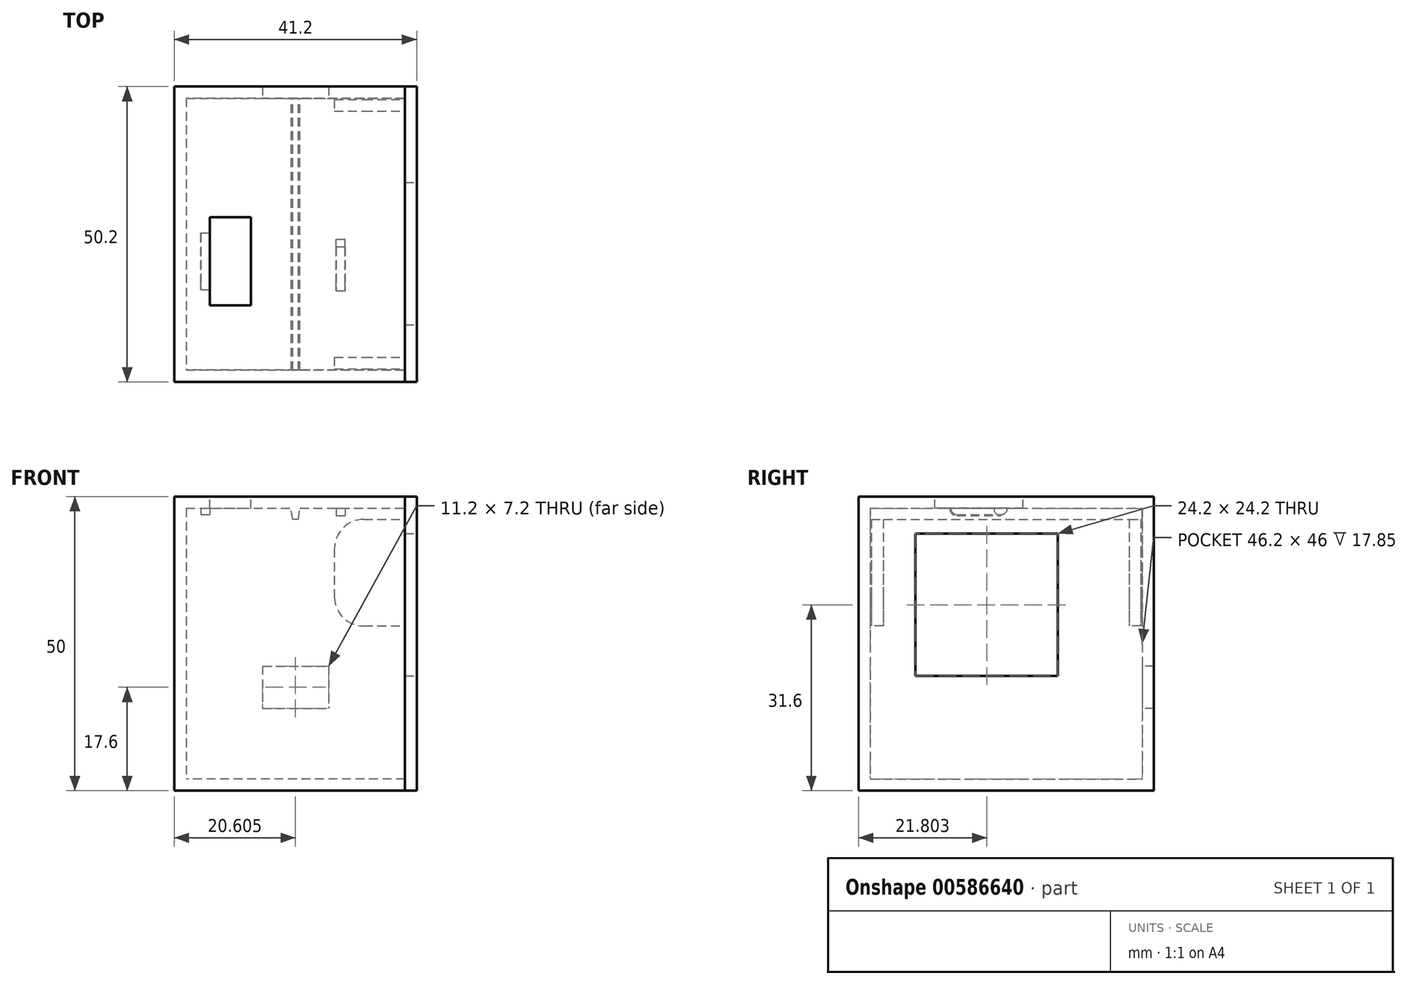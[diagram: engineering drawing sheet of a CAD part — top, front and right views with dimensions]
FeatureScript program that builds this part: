
annotation { "Feature Type Name" : "Feature", "Feature Type Description" : "" }
export const myFeature = defineFeature(function(context is Context, id is Id, definition is map)
    precondition{}
    {
        {
            var Q0;
            Q0=qCreatedBy(makeId("Top.planeOp"),FACE);
            var sketch = newSketch(context, id + "F0", { "sketchPlane" : qUnion([Q0])});
            skLineSegment(sketch, "E0.bottom", {"start": v(-20.75, 21) * mm, "end": v(14.45, 21) * mm});
            skLineSegment(sketch, "E0.top", {"start": v(-20.75, -25.2) * mm, "end": v(14.45, -25.2) * mm});
            skLineSegment(sketch, "E0.left", {"start": v(-20.75, 21) * mm, "end": v(-20.75, -25.2) * mm});
            skLineSegment(sketch, "E0.right", {"start": v(14.45, 21) * mm, "end": v(14.45, -25.2) * mm});
            skLineSegment(sketch, "E1.0", {"start": v(-22.75, -27.2) * mm, "end": v(16.45, -27.2) * mm});
            skLineSegment(sketch, "E1.1", {"start": v(-22.75, 23) * mm, "end": v(-22.75, -27.2) * mm});
            skLineSegment(sketch, "E1.2", {"start": v(-22.75, 23) * mm, "end": v(16.45, 23) * mm});
            skLineSegment(sketch, "E1.3", {"start": v(16.45, 23) * mm, "end": v(16.45, -27.2) * mm});
            skSolve(sketch);
        }
        {
            var Q0;
            Q0=makeQuery(id+"F0.imprint","IMPRINT",FACE,{"disambiguationData":[TD([[makeQuery(id+"F0.imprint","IMPRINT",EDGE,{"derivedFrom":sQuery(id+"F0.wireOp",EDGE,"E0.bottom")}),-1.0]])]});
            var Q1;
            Q1=makeQuery(id+"F0.imprint","IMPRINT",FACE,{"disambiguationData":[TD([[makeQuery(id+"F0.imprint","IMPRINT",EDGE,{"derivedFrom":sQuery(id+"F0.wireOp",EDGE,"E0.bottom")}),1.0]])]});
            extrude(context, id + "F1", {"entities" : qUnion([Q0, Q1]), "depth" : 2 * mm, "offsetDistance" : 25 * mm});
        }
        {
            var Q0;
            Q0=makeQuery(id+"F0.imprint","IMPRINT",FACE,{"disambiguationData":[TD([[makeQuery(id+"F0.imprint","IMPRINT",EDGE,{"derivedFrom":sQuery(id+"F0.wireOp",EDGE,"E0.bottom")}),1.0]])]});
            extrude(context, id + "F2", {"entities" : qUnion([Q0]), "operationType" : NewBodyOperationType.ADD, "depth" : (2 + 46 + 2) * mm, "offsetDistance" : 25 * mm});
        }
        {
            var Q0;
            {var subQ0=sQuery(id+"F0.wireOp",EDGE,"E1.3");Q0=makeQuery(id+"F2.boolean.opBoolean","MERGE",FACE,{"derivedFrom":[makeQuery(id+"F1.opExtrude","SWEPT_FACE",FACE,{"disambiguationData":[OSD([subQ0])]}),makeQuery(id+"F2.opExtrude","SWEPT_FACE",FACE,{"disambiguationData":[OSD([subQ0])]})]});}
            var sketch = newSketch(context, id + "F3", { "sketchPlane" : qUnion([Q0])});
            skLineSegment(sketch, "E2.0", {"start": v(23, 50) * mm, "end": v(-27.2, 50) * mm});
            skLineSegment(sketch, "E2.1", {"start": v(-27.2, 50) * mm, "end": v(-27.2, 0) * mm});
            skLineSegment(sketch, "E2.2", {"start": v(23, 0) * mm, "end": v(-27.2, 0) * mm});
            skLineSegment(sketch, "E2.3", {"start": v(23, 50) * mm, "end": v(23, 0) * mm});
            skLineSegment(sketch, "E3.0", {"start": v(-25.2, 48) * mm, "end": v(-25.2, 2) * mm});
            skLineSegment(sketch, "E3.1", {"start": v(21, 48) * mm, "end": v(-25.2, 48) * mm});
            skLineSegment(sketch, "E3.2", {"start": v(21, 48) * mm, "end": v(21, 2) * mm});
            skLineSegment(sketch, "E3.3", {"start": v(21, 2) * mm, "end": v(-25.2, 2) * mm});
            skLineSegment(sketch, "E4.0", {"start": v(21, 44) * mm, "end": v(-25.2, 44) * mm});
            skSolve(sketch);
        }
        {
            var Q0;
            {var subQ8=sQuery(id+"F3.wireOp",EDGE,"E4.0");Q0=makeQuery(id+"F3.imprint","IMPRINT",FACE,{"disambiguationData":[TD([[makeQuery(id+"F3.imprint","IMPRINT",EDGE,{"derivedFrom":subQ8}),-1.0]])]});}
            var Q1;
            {var subQ0=sQuery(id+"F3.wireOp",EDGE,"E3.3");Q1=makeQuery(id+"F3.imprint","IMPRINT",FACE,{"disambiguationData":[TD([[makeQuery(id+"F3.imprint","IMPRINT",EDGE,{"derivedFrom":subQ0}),-1.0]])]});}
            extrude(context, id + "F4", {"entities" : qUnion([Q0, Q1]), "operationType" : NewBodyOperationType.REMOVE, "oppositeDirection" : true, "depth" : 25 * mm, "offsetDistance" : 25 * mm});
        }
        {
            var Q0;
            Q0=makeQuery(id+"F2.opExtrude","CAP_FACE",FACE,{"disambiguationData":[OSD([sQuery(id+"F0.wireOp",EDGE,"E0.bottom"),sQuery(id+"F0.wireOp",EDGE,"E0.top"),sQuery(id+"F0.wireOp",EDGE,"E0.left"),sQuery(id+"F0.wireOp",EDGE,"E0.right"),sQuery(id+"F0.wireOp",EDGE,"E1.0"),sQuery(id+"F0.wireOp",EDGE,"E1.1"),sQuery(id+"F0.wireOp",EDGE,"E1.2"),sQuery(id+"F0.wireOp",EDGE,"E1.3")])],"isStart":false});
            var sketch = newSketch(context, id + "F5", { "sketchPlane" : qUnion([Q0])});
            skLineSegment(sketch, "E5.0", {"start": v(-20.75, 21) * mm, "end": v(-20.75, -25.2) * mm});
            skLineSegment(sketch, "E5.1", {"start": v(-20.75, -25.2) * mm, "end": v(14.45, -25.2) * mm});
            skLineSegment(sketch, "E5.2", {"start": v(14.45, 21) * mm, "end": v(14.45, -25.2) * mm});
            skLineSegment(sketch, "E5.3", {"start": v(-20.75, 21) * mm, "end": v(14.45, 21) * mm});
            skLineSegment(sketch, "E6.bottom", {"start": v(-16.75, 0.8) * mm, "end": v(-9.75, 0.8) * mm});
            skLineSegment(sketch, "E6.top", {"start": v(-16.75, -14.2) * mm, "end": v(-9.75, -14.2) * mm});
            skLineSegment(sketch, "E6.left", {"start": v(-16.75, 0.8) * mm, "end": v(-16.75, -14.2) * mm});
            skLineSegment(sketch, "E6.right", {"start": v(-9.75, 0.8) * mm, "end": v(-9.75, -14.2) * mm});
            skSolve(sketch);
        }
        {
            var Q0;
            Q0=makeQuery(id+"F5.imprint","IMPRINT",FACE,{"disambiguationData":[TD([[makeQuery(id+"F5.imprint","IMPRINT",EDGE,{"derivedFrom":sQuery(id+"F5.wireOp",EDGE,"E5.0")}),1.0]])]});
            extrude(context, id + "F6", {"entities" : qUnion([Q0]), "operationType" : NewBodyOperationType.ADD, "oppositeDirection" : true, "depth" : 2 * mm, "offsetDistance" : 25 * mm});
        }
        {
            var Q0;
            Q0=makeQuery(id+"F6.opExtrude","SWEPT_FACE",FACE,{"disambiguationData":[OSD([sQuery(id+"F5.wireOp",EDGE,"E6.left")])]});
            var sketch = newSketch(context, id + "F7", { "sketchPlane" : qUnion([Q0])});
            skLineSegment(sketch, "E7.0", {"start": v(0.8, 48) * mm, "end": v(-6.7, 48) * mm});
            skPoint(sketch, "E8", {"position": v(-6.7, 48) * mm});
            skLineSegment(sketch, "E9", {"start": v(-6.7, 48) * mm, "end": v(-14.2, 48) * mm});
            skPoint(sketch, "E10", {"position": v(-10.45, 48) * mm});
            skPoint(sketch, "E11", {"position": v(-2.95, 48) * mm});
            skCircle(sketch, "E12", {"center": v(-10.45, 48) * mm, "radius": 1.05 * mm});
            skLineSegment(sketch, "E13", {"start": v(-6.7, 45.3) * mm, "end": v(-6.7, 50) * mm, "construction": true});
            skCircle(sketch, "E14.MirrorC", {"center": v(-2.95, 48) * mm, "radius": 1.05 * mm});
            skLineSegment(sketch, "E15", {"start": v(-10.45, 48) * mm, "end": v(-10.45, 46.06) * mm, "construction": true});
            skLineSegment(sketch, "E16.MirrorCS", {"start": v(-2.95, 48) * mm, "end": v(-2.95, 46.06) * mm, "construction": true});
            skLineSegment(sketch, "E17", {"start": v(-10.45, 46.95) * mm, "end": v(-2.95, 46.95) * mm});
            skPoint(sketch, "E17.startSnap0", {"position": v(-10.45, 47.03) * mm});
            skSolve(sketch);
        }
        {
            var Q0;
            {var subQ0=sQuery(id+"F7.wireOp",EDGE,"E17");Q0=makeQuery(id+"F7.imprint","IMPRINT",FACE,{"disambiguationData":[TD([[makeQuery(id+"F7.imprint","IMPRINT",EDGE,{"derivedFrom":subQ0}),1.0]])]});}
            var Q1;
            {var subQ0=sQuery(id+"F7.wireOp",EDGE,"E14.MirrorC");var subQ1=sQuery(id+"F7.wireOp",EDGE,"E7.0");var subQ2=makeQuery(id+"F7.imprint","INTERSECT",VERTEX,{"disambiguationData":[OD(0.0)],"derivedFrom":[subQ1,subQ0]});Q1=makeQuery(id+"F7.imprint","IMPRINT",FACE,{"disambiguationData":[TD([[makeQuery(id+"F7.imprint","IMPRINT",EDGE,{"disambiguationData":[TD([[subQ2,-1.0]])],"derivedFrom":subQ1}),1.0]])]});}
            var Q2;
            {var subQ0=sQuery(id+"F7.wireOp",EDGE,"E12");var subQ1=sQuery(id+"F7.wireOp",EDGE,"E9");var subQ2=makeQuery(id+"F7.imprint","INTERSECT",VERTEX,{"disambiguationData":[OD(0.0)],"derivedFrom":[subQ1,subQ0]});Q2=makeQuery(id+"F7.imprint","IMPRINT",FACE,{"disambiguationData":[TD([[makeQuery(id+"F7.imprint","IMPRINT",EDGE,{"disambiguationData":[TD([[subQ2,1.0]])],"derivedFrom":subQ1}),1.0]])]});}
            extrude(context, id + "F8", {"entities" : qUnion([Q0, Q1, Q2]), "operationType" : NewBodyOperationType.ADD, "oppositeDirection" : true, "depth" : 1.5 * mm, "offsetDistance" : 25 * mm});
        }
        {
            var Q0;
            Q0=makeQuery(id+"F4.boolean.opBoolean","MERGE",FACE,{"derivedFrom":[makeQuery(id+"F2.opExtrude","SWEPT_FACE",FACE,{"disambiguationData":[OSD([sQuery(id+"F0.wireOp",EDGE,"E0.bottom")])]}),makeQuery(id+"F4.opExtrude","SWEPT_FACE",FACE,{"disambiguationData":[OSD([sQuery(id+"F3.wireOp",EDGE,"E3.2")])]})]});
            var sketch = newSketch(context, id + "F9", { "sketchPlane" : qUnion([Q0])});
            skPoint(sketch, "E18", {"position": v(-2.15, 48) * mm});
            skLineSegment(sketch, "E19", {"start": v(-2.15, 40.55) * mm, "end": v(-2.15, 51.7) * mm, "construction": true});
            skPoint(sketch, "E20.endSnap0", {"position": v(-2.15, 46.13) * mm});
            skLineSegment(sketch, "E21", {"start": v(-2.15, 46.13) * mm, "end": v(-2.65, 46.13) * mm});
            skLineSegment(sketch, "E22", {"start": v(-2.65, 46.13) * mm, "end": v(-2.9, 48) * mm});
            skLineSegment(sketch, "E23", {"start": v(-2.9, 48) * mm, "end": v(-2.15, 48) * mm});
            skLineSegment(sketch, "E24.MirrorCS", {"start": v(-2.15, 46.13) * mm, "end": v(-1.65, 46.13) * mm});
            skLineSegment(sketch, "E25.MirrorCS", {"start": v(-1.4, 48) * mm, "end": v(-2.15, 48) * mm});
            skLineSegment(sketch, "E26.MirrorCS", {"start": v(-1.65, 46.13) * mm, "end": v(-1.4, 48) * mm});
            skSolve(sketch);
        }
        {
            var Q0;
            Q0=makeQuery(id+"F9.imprint","IMPRINT",FACE,{"disambiguationData":[TD([[makeQuery(id+"F9.imprint","IMPRINT",EDGE,{"derivedFrom":sQuery(id+"F9.wireOp",EDGE,"E21")}),-1.0]])]});
            extrude(context, id + "F10", {"entities" : qUnion([Q0]), "operationType" : NewBodyOperationType.ADD, "endBound" : BoundingType.UP_TO_NEXT, "depth" : 25 * mm, "offsetDistance" : 25 * mm});
        }
        {
            var Q0;
            {var subQ0=sQuery(id+"F0.wireOp",EDGE,"E1.3");Q0=makeQuery(id+"F2.boolean.opBoolean","MERGE",FACE,{"derivedFrom":[makeQuery(id+"F1.opExtrude","SWEPT_FACE",FACE,{"disambiguationData":[OSD([subQ0])]}),makeQuery(id+"F2.opExtrude","SWEPT_FACE",FACE,{"disambiguationData":[OSD([subQ0])]})]});}
            var sketch = newSketch(context, id + "F11", { "sketchPlane" : qUnion([Q0])});
            skLineSegment(sketch, "E27.0", {"start": v(-27.2, 50) * mm, "end": v(-27.2, 0) * mm});
            skLineSegment(sketch, "E27.1", {"start": v(23, 50) * mm, "end": v(-27.2, 50) * mm});
            skLineSegment(sketch, "E27.2", {"start": v(23, 50) * mm, "end": v(23, 0) * mm});
            skLineSegment(sketch, "E27.3", {"start": v(23, 0) * mm, "end": v(-27.2, 0) * mm});
            skLineSegment(sketch, "E27.4", {"start": v(21, 48) * mm, "end": v(21, 2) * mm});
            skLineSegment(sketch, "E27.5", {"start": v(21, 48) * mm, "end": v(-25.2, 48) * mm});
            skLineSegment(sketch, "E27.6", {"start": v(-25.2, 48) * mm, "end": v(-25.2, 2) * mm});
            skLineSegment(sketch, "E27.7", {"start": v(-25.2, 2) * mm, "end": v(21, 2) * mm});
            skLineSegment(sketch, "E28", {"start": v(21, 28) * mm, "end": v(-25.2, 28) * mm});
            skLineSegment(sketch, "E29", {"start": v(-25, 48) * mm, "end": v(-25, 28) * mm});
            skLineSegment(sketch, "E30", {"start": v(-2.1, 18.33) * mm, "end": v(-2.1, 38.94) * mm, "construction": true});
            skPoint(sketch, "E30.startSnap0", {"position": v(-2.1, 28) * mm});
            skLineSegment(sketch, "E31.MirrorCS", {"start": v(20.8, 48) * mm, "end": v(20.8, 28) * mm});
            skLineSegment(sketch, "E32", {"start": v(-23, 48) * mm, "end": v(-23, 28) * mm});
            skLineSegment(sketch, "E33.MirrorCS", {"start": v(18.8, 48) * mm, "end": v(18.8, 28) * mm});
            skLineSegment(sketch, "E34.0", {"start": v(-25.2, 46.13) * mm, "end": v(21, 46.13) * mm});
            skSolve(sketch);
        }
        {
            var Q0;
            {var subQ1=sQuery(id+"F11.wireOp",EDGE,"E32");var subQ5=sQuery(id+"F11.wireOp",EDGE,"E28");var subQ6=makeQuery(id+"F11.imprint","INTERSECT",VERTEX,{"derivedFrom":[subQ5,subQ1]});Q0=makeQuery(id+"F11.imprint","IMPRINT",FACE,{"disambiguationData":[TD([[makeQuery(id+"F11.imprint","IMPRINT",EDGE,{"disambiguationData":[TD([[subQ6,1.0]])],"derivedFrom":subQ5}),-1.0]])]});}
            var Q1;
            {var subQ0=sQuery(id+"F11.wireOp",EDGE,"E27.5");var subQ1=makeQuery(id+"F4.boolean.opBoolean","COPY",EDGE,{"derivedFrom":makeQuery(id+"F4.opExtrude","CAP_EDGE",EDGE,{"disambiguationData":[OSD([sQuery(id+"F3.wireOp",EDGE,"MNPgkXDO-O9Mw-NbgN-yxrE-MuUepim71a7d")])],"isStart":true})});var subQ2=makeQuery(id+"F11.imprint","INTERSECT",VERTEX,{"disambiguationData":[OD(1.0)],"derivedFrom":[subQ1,subQ0]});Q1=makeQuery(id+"F11.imprint","IMPRINT",FACE,{"disambiguationData":[TD([[makeQuery(id+"F11.imprint","IMPRINT",EDGE,{"disambiguationData":[TD([[subQ2,-1.0]])],"derivedFrom":subQ0}),1.0]])]});}
            var Q2;
            {var subQ0=sQuery(id+"F11.wireOp",EDGE,"E27.5");var subQ1=makeQuery(id+"F4.boolean.opBoolean","COPY",EDGE,{"derivedFrom":makeQuery(id+"F4.opExtrude","CAP_EDGE",EDGE,{"disambiguationData":[OSD([sQuery(id+"F3.wireOp",EDGE,"MNPgkXDO-O9Mw-NbgN-yxrE-MuUepim71a7d")])],"isStart":true})});var subQ2=makeQuery(id+"F11.imprint","INTERSECT",VERTEX,{"disambiguationData":[OD(0.0)],"derivedFrom":[subQ1,subQ0]});Q2=makeQuery(id+"F11.imprint","IMPRINT",FACE,{"disambiguationData":[TD([[makeQuery(id+"F11.imprint","IMPRINT",EDGE,{"disambiguationData":[TD([[subQ2,1.0]])],"derivedFrom":subQ0}),1.0]])]});}
            var Q3;
            {var subQ0=sQuery(id+"F11.wireOp",EDGE,"E34.0");var subQ1=makeQuery(id+"F4.boolean.opBoolean","COPY",EDGE,{"derivedFrom":makeQuery(id+"F4.opExtrude","CAP_EDGE",EDGE,{"disambiguationData":[OSD([sQuery(id+"F3.wireOp",EDGE,"MNPgkXDO-O9Mw-NbgN-yxrE-MuUepim71a7d")])],"isStart":true})});var subQ2=makeQuery(id+"F11.imprint","INTERSECT",VERTEX,{"disambiguationData":[OD(0.0)],"derivedFrom":[subQ1,subQ0]});Q3=makeQuery(id+"F11.imprint","IMPRINT",FACE,{"disambiguationData":[TD([[makeQuery(id+"F11.imprint","IMPRINT",EDGE,{"disambiguationData":[TD([[subQ2,-1.0]])],"derivedFrom":subQ0}),-1.0]])]});}
            var Q4;
            Q4=makeQuery(id+"F11.imprint","IMPRINT",FACE,{"disambiguationData":[TD([[makeQuery(id+"F11.imprint","IMPRINT",EDGE,{"derivedFrom":sQuery(id+"F11.wireOp",EDGE,"E27.0")}),1.0]])]});
            var Q5;
            {var subQ4=sQuery(id+"F11.wireOp",EDGE,"E27.7");Q5=makeQuery(id+"F11.imprint","IMPRINT",FACE,{"disambiguationData":[TD([[makeQuery(id+"F11.imprint","IMPRINT",EDGE,{"derivedFrom":subQ4}),-1.0]])]});}
            var Q6;
            {var subQ0=sQuery(id+"F11.wireOp",EDGE,"E28");var subQ1=sQuery(id+"F11.wireOp",EDGE,"E27.4");var subQ2=makeQuery(id+"F11.imprint","INTERSECT",VERTEX,{"derivedFrom":[subQ1,subQ0]});Q6=makeQuery(id+"F11.imprint","IMPRINT",FACE,{"disambiguationData":[TD([[makeQuery(id+"F11.imprint","IMPRINT",EDGE,{"disambiguationData":[TD([[subQ2,1.0]])],"derivedFrom":subQ1}),-1.0]])]});}
            var Q7;
            {var subQ0=sQuery(id+"F11.wireOp",EDGE,"E27.5");var subQ1=makeQuery(id+"F4.boolean.opBoolean","COPY",EDGE,{"derivedFrom":makeQuery(id+"F4.opExtrude","CAP_EDGE",EDGE,{"disambiguationData":[OSD([sQuery(id+"F3.wireOp",EDGE,"MNPgkXDO-O9Mw-NbgN-yxrE-MuUepim71a7d")])],"isStart":true})});var subQ2=makeQuery(id+"F11.imprint","INTERSECT",VERTEX,{"disambiguationData":[OD(0.0)],"derivedFrom":[subQ1,subQ0]});Q7=makeQuery(id+"F11.imprint","IMPRINT",FACE,{"disambiguationData":[TD([[makeQuery(id+"F11.imprint","IMPRINT",EDGE,{"disambiguationData":[TD([[subQ2,-1.0]])],"derivedFrom":subQ0}),1.0]])]});}
            var Q8;
            {var subQ0=sQuery(id+"F11.wireOp",EDGE,"E29");var subQ1=sQuery(id+"F11.wireOp",EDGE,"E28");var subQ2=makeQuery(id+"F11.imprint","INTERSECT",VERTEX,{"derivedFrom":[subQ1,subQ0]});Q8=makeQuery(id+"F11.imprint","IMPRINT",FACE,{"disambiguationData":[TD([[makeQuery(id+"F11.imprint","IMPRINT",EDGE,{"disambiguationData":[TD([[subQ2,1.0]])],"derivedFrom":subQ1}),-1.0]])]});}
            var Q9;
            {var subQ0=sQuery(id+"F11.wireOp",EDGE,"E31.MirrorCS");var subQ1=sQuery(id+"F11.wireOp",EDGE,"E28");var subQ2=makeQuery(id+"F11.imprint","INTERSECT",VERTEX,{"derivedFrom":[subQ1,subQ0]});Q9=makeQuery(id+"F11.imprint","IMPRINT",FACE,{"disambiguationData":[TD([[makeQuery(id+"F11.imprint","IMPRINT",EDGE,{"disambiguationData":[TD([[subQ2,-1.0]])],"derivedFrom":subQ1}),-1.0]])]});}
            var Q10;
            {var subQ0=sQuery(id+"F11.wireOp",EDGE,"E28");var subQ1=sQuery(id+"F11.wireOp",EDGE,"E27.6");var subQ2=makeQuery(id+"F11.imprint","INTERSECT",VERTEX,{"derivedFrom":[subQ1,subQ0]});Q10=makeQuery(id+"F11.imprint","IMPRINT",FACE,{"disambiguationData":[TD([[makeQuery(id+"F11.imprint","IMPRINT",EDGE,{"disambiguationData":[TD([[subQ2,1.0]])],"derivedFrom":subQ1}),1.0]])]});}
            var Q11;
            {var subQ0=sQuery(id+"F11.wireOp",EDGE,"E31.MirrorCS");var subQ1=sQuery(id+"F11.wireOp",EDGE,"E27.5");var subQ2=makeQuery(id+"F11.imprint","INTERSECT",VERTEX,{"derivedFrom":[subQ1,subQ0]});Q11=makeQuery(id+"F11.imprint","IMPRINT",FACE,{"disambiguationData":[TD([[makeQuery(id+"F11.imprint","IMPRINT",EDGE,{"disambiguationData":[TD([[subQ2,-1.0]])],"derivedFrom":subQ1}),1.0]])]});}
            var Q12;
            {var subQ0=sQuery(id+"F11.wireOp",EDGE,"E27.5");var subQ1=sQuery(id+"F11.wireOp",EDGE,"E27.4");var subQ2=makeQuery(id+"F11.imprint","INTERSECT",VERTEX,{"derivedFrom":[subQ1,subQ0]});Q12=makeQuery(id+"F11.imprint","IMPRINT",FACE,{"disambiguationData":[TD([[makeQuery(id+"F11.imprint","IMPRINT",EDGE,{"disambiguationData":[TD([[subQ2,-1.0]])],"derivedFrom":subQ1}),-1.0]])]});}
            var Q13;
            {var subQ0=sQuery(id+"F11.wireOp",EDGE,"E27.6");var subQ1=sQuery(id+"F11.wireOp",EDGE,"E27.5");var subQ2=makeQuery(id+"F11.imprint","INTERSECT",VERTEX,{"derivedFrom":[subQ1,subQ0]});Q13=makeQuery(id+"F11.imprint","IMPRINT",FACE,{"disambiguationData":[TD([[makeQuery(id+"F11.imprint","IMPRINT",EDGE,{"disambiguationData":[TD([[subQ2,1.0]])],"derivedFrom":subQ1}),1.0]])]});}
            var Q14;
            {var subQ0=sQuery(id+"F11.wireOp",EDGE,"E29");var subQ1=sQuery(id+"F11.wireOp",EDGE,"E27.5");var subQ2=makeQuery(id+"F11.imprint","INTERSECT",VERTEX,{"derivedFrom":[subQ1,subQ0]});Q14=makeQuery(id+"F11.imprint","IMPRINT",FACE,{"disambiguationData":[TD([[makeQuery(id+"F11.imprint","IMPRINT",EDGE,{"disambiguationData":[TD([[subQ2,1.0]])],"derivedFrom":subQ1}),1.0]])]});}
            extrude(context, id + "F12", {"entities" : qUnion([Q0, Q1, Q2, Q3, Q4, Q5, Q6, Q7, Q8, Q9, Q10, Q11, Q12, Q13, Q14]), "depth" : 2 * mm, "offsetDistance" : 25 * mm});
        }
        {
            var Q0;
            {var subQ0=sQuery(id+"F11.wireOp",EDGE,"E31.MirrorCS");var subQ1=sQuery(id+"F11.wireOp",EDGE,"E28");var subQ2=makeQuery(id+"F11.imprint","INTERSECT",VERTEX,{"derivedFrom":[subQ1,subQ0]});Q0=makeQuery(id+"F11.imprint","IMPRINT",FACE,{"disambiguationData":[TD([[makeQuery(id+"F11.imprint","IMPRINT",EDGE,{"disambiguationData":[TD([[subQ2,-1.0]])],"derivedFrom":subQ1}),-1.0]])]});}
            var Q1;
            {var subQ0=sQuery(id+"F11.wireOp",EDGE,"E29");var subQ1=sQuery(id+"F11.wireOp",EDGE,"E28");var subQ2=makeQuery(id+"F11.imprint","INTERSECT",VERTEX,{"derivedFrom":[subQ1,subQ0]});Q1=makeQuery(id+"F11.imprint","IMPRINT",FACE,{"disambiguationData":[TD([[makeQuery(id+"F11.imprint","IMPRINT",EDGE,{"disambiguationData":[TD([[subQ2,1.0]])],"derivedFrom":subQ1}),-1.0]])]});}
            extrude(context, id + "F13", {"entities" : qUnion([Q0, Q1]), "operationType" : NewBodyOperationType.ADD, "oppositeDirection" : true, "depth" : 12 * mm, "offsetDistance" : 25 * mm});
        }
        {
            var Q0;
            {var subQ0=sQuery(id+"F11.wireOp",EDGE,"E34.0");Q0=makeQuery(id+"F13.opExtrude","CAP_EDGE",EDGE,{"disambiguationData":[OSD([subQ0]),TDD([makeQuery(id+"F11.imprint","IMPRINT",EDGE,{"disambiguationData":[TD([[makeQuery(id+"F11.imprint","INTERSECT",VERTEX,{"derivedFrom":[sQuery(id+"F11.wireOp",EDGE,"E31.MirrorCS"),subQ0]}),1.0]])],"derivedFrom":subQ0})])],"isStart":false});}
            var Q1;
            {var subQ0=sQuery(id+"F11.wireOp",EDGE,"E34.0");Q1=makeQuery(id+"F13.opExtrude","CAP_EDGE",EDGE,{"disambiguationData":[OSD([subQ0]),TDD([makeQuery(id+"F11.imprint","IMPRINT",EDGE,{"disambiguationData":[TD([[makeQuery(id+"F11.imprint","INTERSECT",VERTEX,{"derivedFrom":[sQuery(id+"F11.wireOp",EDGE,"E29"),subQ0]}),-1.0]])],"derivedFrom":subQ0})])],"isStart":false});}
            var Q2;
            {var subQ0=sQuery(id+"F11.wireOp",EDGE,"E28");Q2=makeQuery(id+"F13.opExtrude","CAP_EDGE",EDGE,{"disambiguationData":[OSD([subQ0]),TDD([makeQuery(id+"F11.imprint","IMPRINT",EDGE,{"disambiguationData":[TD([[makeQuery(id+"F11.imprint","INTERSECT",VERTEX,{"derivedFrom":[subQ0,sQuery(id+"F11.wireOp",EDGE,"E29")]}),1.0]])],"derivedFrom":subQ0})])],"isStart":false});}
            var Q3;
            {var subQ0=sQuery(id+"F11.wireOp",EDGE,"E28");Q3=makeQuery(id+"F13.opExtrude","CAP_EDGE",EDGE,{"disambiguationData":[OSD([subQ0]),TDD([makeQuery(id+"F11.imprint","IMPRINT",EDGE,{"disambiguationData":[TD([[makeQuery(id+"F11.imprint","INTERSECT",VERTEX,{"derivedFrom":[subQ0,sQuery(id+"F11.wireOp",EDGE,"E31.MirrorCS")]}),-1.0]])],"derivedFrom":subQ0})])],"isStart":false});}
            fillet(context, id + "F14", {"entities" : qUnion([Q0, Q1, Q2, Q3]), "radius" : 5 * mm, "tangentPropagation" : true, "allowEdgeOverflow" : false});
        }
        {
            var Q0;
            Q0=makeQuery(id+"F12.opExtrude","CAP_FACE",FACE,{"disambiguationData":[OSD([sQuery(id+"F11.wireOp",EDGE,"E27.0"),sQuery(id+"F11.wireOp",EDGE,"E27.1"),sQuery(id+"F11.wireOp",EDGE,"E27.2"),sQuery(id+"F11.wireOp",EDGE,"E27.3")])],"isStart":false});
            var sketch = newSketch(context, id + "F15", { "sketchPlane" : qUnion([Q0])});
            skLineSegment(sketch, "E35.0", {"start": v(-27.2, 50) * mm, "end": v(-27.2, 0) * mm});
            skLineSegment(sketch, "E35.1", {"start": v(23, 50) * mm, "end": v(-27.2, 50) * mm});
            skLineSegment(sketch, "E35.2", {"start": v(23, 50) * mm, "end": v(23, 0) * mm});
            skLineSegment(sketch, "E35.3", {"start": v(23, 0) * mm, "end": v(-27.2, 0) * mm});
            skLineSegment(sketch, "E36.bottom", {"start": v(-17.5, 43.7) * mm, "end": v(6.7, 43.7) * mm});
            skLineSegment(sketch, "E36.top", {"start": v(-17.5, 19.5) * mm, "end": v(6.7, 19.5) * mm});
            skLineSegment(sketch, "E36.left", {"start": v(-17.5, 43.7) * mm, "end": v(-17.5, 19.5) * mm});
            skLineSegment(sketch, "E36.right", {"start": v(6.7, 43.7) * mm, "end": v(6.7, 19.5) * mm});
            skSolve(sketch);
        }
        {
            var Q0;
            Q0=makeQuery(id+"F15.imprint","IMPRINT",FACE,{"disambiguationData":[TD([[makeQuery(id+"F15.imprint","IMPRINT",EDGE,{"derivedFrom":sQuery(id+"F15.wireOp",EDGE,"E36.bottom")}),-1.0]])]});
            extrude(context, id + "F16", {"entities" : qUnion([Q0]), "operationType" : NewBodyOperationType.REMOVE, "oppositeDirection" : true, "depth" : 5 * mm, "offsetDistance" : 25 * mm});
        }
        {
            var Q0;
            Q0=makeQuery(id+"F4.boolean.opBoolean","MERGE",FACE,{"derivedFrom":[makeQuery(id+"F2.opExtrude","SWEPT_FACE",FACE,{"disambiguationData":[OSD([sQuery(id+"F0.wireOp",EDGE,"E0.bottom")])]}),makeQuery(id+"F4.opExtrude","SWEPT_FACE",FACE,{"disambiguationData":[OSD([sQuery(id+"F3.wireOp",EDGE,"E3.2")])]})]});
            var sketch = newSketch(context, id + "F17", { "sketchPlane" : qUnion([Q0])});
            skLineSegment(sketch, "E37.0", {"start": v(16.45, 48) * mm, "end": v(16.45, 2) * mm});
            skLineSegment(sketch, "E37.1", {"start": v(-20.75, 48) * mm, "end": v(-20.75, 2) * mm});
            skLineSegment(sketch, "E37.2", {"start": v(16.45, 2) * mm, "end": v(-20.75, 2) * mm});
            skLineSegment(sketch, "E38.bottom", {"start": v(-7.75, 21.2) * mm, "end": v(3.45, 21.2) * mm});
            skLineSegment(sketch, "E38.top", {"start": v(-7.75, 14) * mm, "end": v(3.45, 14) * mm});
            skLineSegment(sketch, "E38.left", {"start": v(-7.75, 21.2) * mm, "end": v(-7.75, 14) * mm});
            skLineSegment(sketch, "E38.right", {"start": v(3.45, 21.2) * mm, "end": v(3.45, 14) * mm});
            skPoint(sketch, "E39", {"position": v(-2.15, 2) * mm});
            skPoint(sketch, "E40", {"position": v(-2.15, 14) * mm});
            skLineSegment(sketch, "E41", {"start": v(-2.15, -8.23) * mm, "end": v(-2.15, 37.44) * mm, "construction": true});
            skSolve(sketch);
        }
        {
            var Q0;
            Q0=makeQuery(id+"F17.imprint","IMPRINT",FACE,{"disambiguationData":[TD([[makeQuery(id+"F17.imprint","IMPRINT",EDGE,{"derivedFrom":sQuery(id+"F17.wireOp",EDGE,"E38.bottom")}),-1.0]])]});
            extrude(context, id + "F18", {"entities" : qUnion([Q0]), "operationType" : NewBodyOperationType.REMOVE, "oppositeDirection" : true, "depth" : 4.5 * mm, "offsetDistance" : 25 * mm});
        }
        {
            var Q0;
            {var subQ0=sQuery(id+"F0.wireOp",EDGE,"E1.3");Q0=makeQuery(id+"F2.boolean.opBoolean","MERGE",FACE,{"derivedFrom":[makeQuery(id+"F1.opExtrude","SWEPT_FACE",FACE,{"disambiguationData":[OSD([subQ0])]}),makeQuery(id+"F2.opExtrude","SWEPT_FACE",FACE,{"disambiguationData":[OSD([subQ0])]})]});}
            var sketch = newSketch(context, id + "F19", { "sketchPlane" : qUnion([Q0])});
            skCircle(sketch, "E42.1", {"center": v(-2.95, 48) * mm, "radius": 1.25 * mm});
            skLineSegment(sketch, "E42.2", {"start": v(0.8, 48) * mm, "end": v(-6.7, 48) * mm});
            skLineSegment(sketch, "E42.3", {"start": v(-6.7, 48) * mm, "end": v(-14.2, 48) * mm});
            skCircle(sketch, "E42.4", {"center": v(-10.45, 48) * mm, "radius": 1.25 * mm});
            skPoint(sketch, "E43", {"position": v(-10.45, 46.75) * mm});
            skPoint(sketch, "E44", {"position": v(-2.95, 46.75) * mm});
            skLineSegment(sketch, "E45", {"start": v(-10.45, 46.75) * mm, "end": v(-2.95, 46.75) * mm});
            skSolve(sketch);
        }
        {
            var Q0;
            {var subQ0=sQuery(id+"F19.wireOp",EDGE,"E42.4");var subQ1=sQuery(id+"F19.wireOp",EDGE,"E42.3");var subQ2=makeQuery(id+"F19.imprint","INTERSECT",VERTEX,{"disambiguationData":[OD(0.0)],"derivedFrom":[subQ1,subQ0]});Q0=makeQuery(id+"F19.imprint","IMPRINT",FACE,{"disambiguationData":[TD([[makeQuery(id+"F19.imprint","IMPRINT",EDGE,{"disambiguationData":[TD([[subQ2,-1.0]])],"derivedFrom":subQ1}),1.0]])]});}
            var Q1;
            {var subQ5=sQuery(id+"F19.wireOp",EDGE,"E45");Q1=makeQuery(id+"F19.imprint","IMPRINT",FACE,{"disambiguationData":[TD([[makeQuery(id+"F19.imprint","IMPRINT",EDGE,{"derivedFrom":subQ5}),1.0]])]});}
            var Q2;
            {var subQ0=sQuery(id+"F19.wireOp",EDGE,"E42.1");var subQ1=makeQuery(id+"F19.imprint","INTERSECT",VERTEX,{"derivedFrom":[subQ0,sQuery(id+"F19.wireOp",EDGE,"E45")]});Q2=makeQuery(id+"F19.imprint","IMPRINT",FACE,{"disambiguationData":[TD([[makeQuery(id+"F19.imprint","IMPRINT",EDGE,{"disambiguationData":[TD([[subQ1,1.0]])],"derivedFrom":subQ0}),-1.0]])]});}
            extrude(context, id + "F20", {"entities" : qUnion([Q0, Q1, Q2]), "operationType" : NewBodyOperationType.ADD, "oppositeDirection" : true, "depth" : (10.2 + 1.5) * mm, "offsetDistance" : 25 * mm, "hasSecondDirection" : true, "secondDirectionOppositeDirection" : true, "secondDirectionDepth" : 10.2 * mm});
        }
    });
